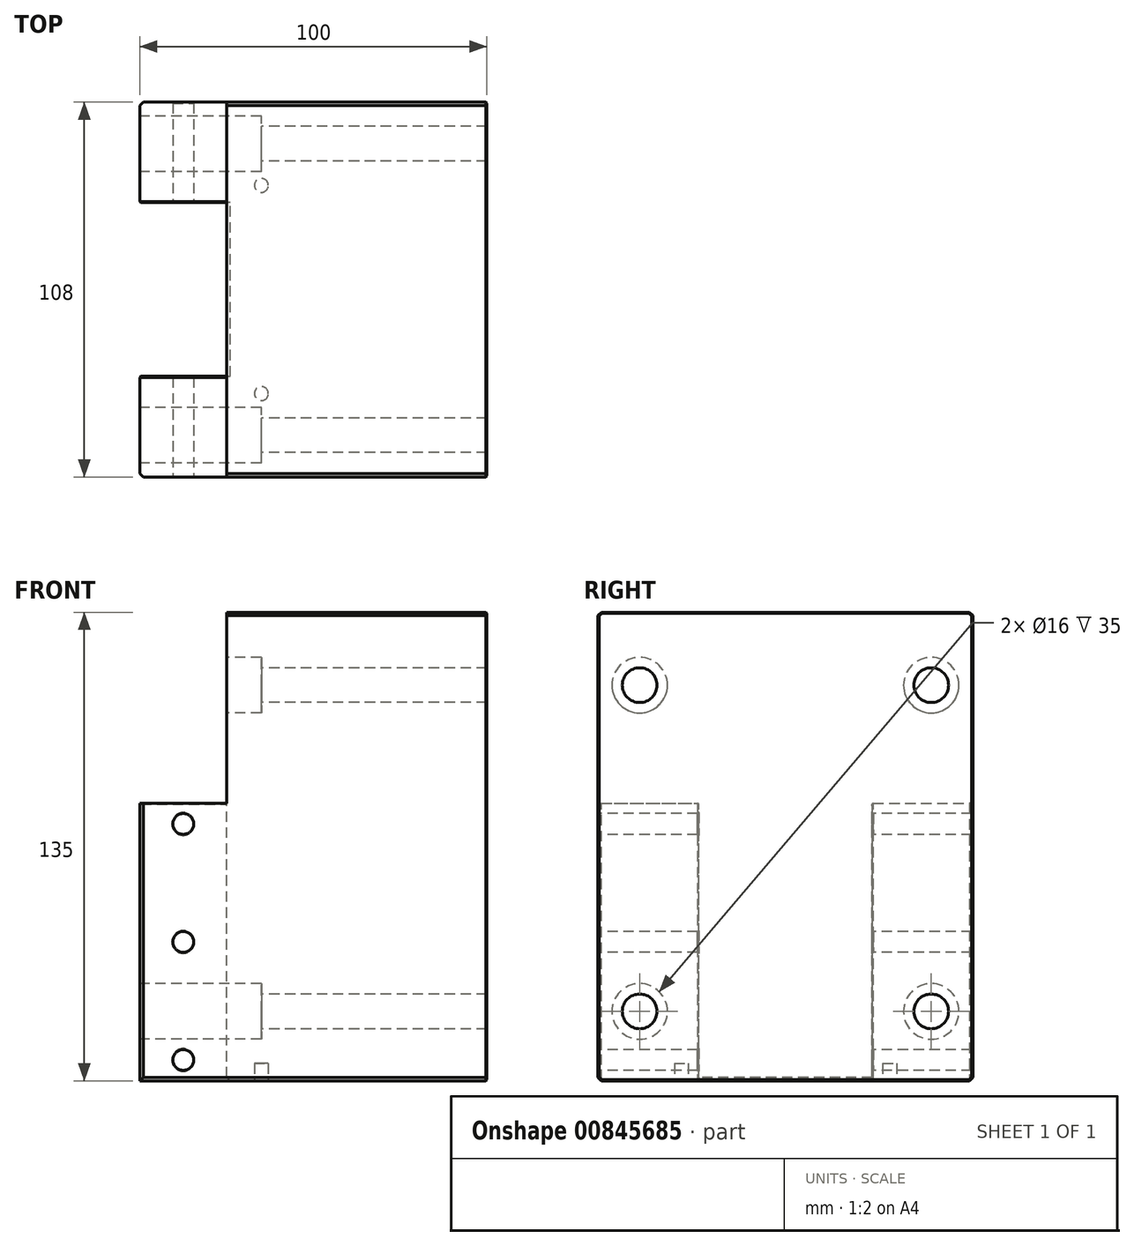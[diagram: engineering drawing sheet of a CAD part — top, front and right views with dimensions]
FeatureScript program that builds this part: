
annotation { "Feature Type Name" : "Feature", "Feature Type Description" : "" }
export const myFeature = defineFeature(function(context is Context, id is Id, definition is map)
    precondition{}
    {
        {
            var Q0;
            Q0=qCreatedBy(makeId("Front.planeOp"),FACE);
            var sketch = newSketch(context, id + "F0", { "sketchPlane" : qUnion([Q0])});
            skLineSegment(sketch, "E0.bottom", {"start": v(-100, -50) * mm, "end": v(-100, 58) * mm});
            skLineSegment(sketch, "E0.top", {"start": v(0, -50) * mm, "end": v(0, -21) * mm});
            skLineSegment(sketch, "E0.left", {"start": v(-100, -50) * mm, "end": v(0, -50) * mm});
            skLineSegment(sketch, "E0.right", {"start": v(-100, 58) * mm, "end": v(0, 58) * mm});
            skLineSegment(sketch, "E1", {"start": v(0, -21) * mm, "end": v(-25, -21) * mm});
            skLineSegment(sketch, "E2", {"start": v(-25, -21) * mm, "end": v(-25, 29) * mm});
            skLineSegment(sketch, "E3", {"start": v(-25, 29) * mm, "end": v(0, 29) * mm});
            skLineSegment(sketch, "E4.trimOffspring", {"start": v(0, 29) * mm, "end": v(0, 58) * mm});
            skLineSegment(sketch, "E5", {"start": v(0, -21) * mm, "end": v(0, 29) * mm, "construction": true});
            skSolve(sketch);
        }
        {
            var Q0;
            Q0 = qSketchRegion(id + "F0", true);
            extrude(context, id + "F1", {"entities" : qUnion([Q0]), "depth" : 135 * mm, "offsetDistance" : 25 * mm});
        }
        {
            var Q0;
            Q0=makeQuery(id+"F1.opExtrude","CAP_FACE",FACE,{"disambiguationData":[OSD([sQuery(id+"F0.wireOp",EDGE,"E0.bottom"),sQuery(id+"F0.wireOp",EDGE,"E0.top"),sQuery(id+"F0.wireOp",EDGE,"E0.left"),sQuery(id+"F0.wireOp",EDGE,"E0.right"),sQuery(id+"F0.wireOp",EDGE,"E1"),sQuery(id+"F0.wireOp",EDGE,"E2"),sQuery(id+"F0.wireOp",EDGE,"E3"),sQuery(id+"F0.wireOp",EDGE,"E4.trimOffspring")])],"isStart":true});
            var sketch = newSketch(context, id + "F2", { "sketchPlane" : qUnion([Q0])});
            skPoint(sketch, "E6.oppositeSnap0", {"position": v(25, 0) * mm});
            skLineSegment(sketch, "E6.bottom", {"start": v(0, -50) * mm, "end": v(0, 58) * mm});
            skLineSegment(sketch, "E6.top", {"start": v(25, -50) * mm, "end": v(25, 58) * mm});
            skLineSegment(sketch, "E6.left", {"start": v(25, -50) * mm, "end": v(0, -50) * mm});
            skLineSegment(sketch, "E6.right", {"start": v(25, 58) * mm, "end": v(0, 58) * mm});
            skSolve(sketch);
        }
        {
            var Q0;
            Q0 = qSketchRegion(id + "F2", true);
            extrude(context, id + "F3", {"entities" : qUnion([Q0]), "operationType" : NewBodyOperationType.REMOVE, "oppositeDirection" : true, "depth" : 55 * mm, "offsetDistance" : 25 * mm});
        }
        {
            var Q0;
            Q0=makeQuery(id+"F1.opExtrude","SWEPT_FACE",FACE,{"disambiguationData":[OSD([sQuery(id+"F0.wireOp",EDGE,"E0.top")])]});
            var sketch = newSketch(context, id + "F4", { "sketchPlane" : qUnion([Q0])});
            skCircle(sketch, "E7", {"center": v(-21, -38) * mm, "radius": 8 * mm});
            skCircle(sketch, "E8", {"center": v(-21, 46) * mm, "radius": 8 * mm});
            skCircle(sketch, "E9", {"center": v(-115, -38) * mm, "radius": 8 * mm});
            skCircle(sketch, "E10", {"center": v(-115, 46) * mm, "radius": 8 * mm});
            skLineSegment(sketch, "E11", {"start": v(-21, -38) * mm, "end": v(-115, -38) * mm, "construction": true});
            skLineSegment(sketch, "E12", {"start": v(-21, -38) * mm, "end": v(-21, 46) * mm, "construction": true});
            skLineSegment(sketch, "E13", {"start": v(-21, 46) * mm, "end": v(-115, 46) * mm, "construction": true});
            skLineSegment(sketch, "E14", {"start": v(-115, -38) * mm, "end": v(-115, 82.74) * mm, "construction": true});
            skSolve(sketch);
        }
        {
            var Q0;
            Q0 = qSketchRegion(id + "F4", true);
            extrude(context, id + "F5", {"entities" : qUnion([Q0]), "operationType" : NewBodyOperationType.REMOVE, "oppositeDirection" : true, "depth" : 35 * mm, "offsetDistance" : 25 * mm});
        }
        {
            var Q0;
            Q0=makeQuery(id+"F1.opExtrude","SWEPT_FACE",FACE,{"disambiguationData":[OSD([sQuery(id+"F0.wireOp",EDGE,"E0.left")])]});
            var sketch = newSketch(context, id + "F6", { "sketchPlane" : qUnion([Q0])});
            skPoint(sketch, "E15", {"position": v(-12.5, 61) * mm});
            skLineSegment(sketch, "E16", {"start": v(-12.5, 61) * mm, "end": v(-12.5, 68.08) * mm, "construction": true});
            skPoint(sketch, "E17", {"position": v(-12.5, 95) * mm});
            skPoint(sketch, "E18", {"position": v(-12.5, 129) * mm});
            skCircle(sketch, "E19", {"center": v(-12.5, 61) * mm, "radius": 3 * mm});
            skCircle(sketch, "E20", {"center": v(-12.5, 95) * mm, "radius": 3 * mm});
            skCircle(sketch, "E21", {"center": v(-12.5, 129) * mm, "radius": 3 * mm});
            skSolve(sketch);
        }
        {
            var Q0;
            Q0 = qSketchRegion(id + "F6", true);
            extrude(context, id + "F7", {"entities" : qUnion([Q0]), "operationType" : NewBodyOperationType.REMOVE, "endBound" : BoundingType.THROUGH_ALL, "oppositeDirection" : true, "depth" : 25 * mm, "offsetDistance" : 25 * mm});
        }
        {
            var Q0;
            Q0=makeQuery(id+"F1.opExtrude","CAP_FACE",FACE,{"disambiguationData":[OSD([sQuery(id+"F0.wireOp",EDGE,"E0.bottom"),sQuery(id+"F0.wireOp",EDGE,"E0.top"),sQuery(id+"F0.wireOp",EDGE,"E0.left"),sQuery(id+"F0.wireOp",EDGE,"E0.right"),sQuery(id+"F0.wireOp",EDGE,"E1"),sQuery(id+"F0.wireOp",EDGE,"E2"),sQuery(id+"F0.wireOp",EDGE,"E3"),sQuery(id+"F0.wireOp",EDGE,"E4.trimOffspring")])],"isStart":false});
            var sketch = newSketch(context, id + "F8", { "sketchPlane" : qUnion([Q0])});
            skLineSegment(sketch, "E22", {"start": v(-35, 34) * mm, "end": v(-35, -26) * mm, "construction": true});
            skPoint(sketch, "E23", {"position": v(-35, -26) * mm});
            skPoint(sketch, "E24", {"position": v(-35, 34) * mm});
            skCircle(sketch, "E25", {"center": v(-35, -26) * mm, "radius": 2 * mm});
            skCircle(sketch, "E26", {"center": v(-35, 34) * mm, "radius": 2 * mm});
            skSolve(sketch);
        }
        {
            var Q0;
            Q0 = qSketchRegion(id + "F8", true);
            extrude(context, id + "F9", {"entities" : qUnion([Q0]), "operationType" : NewBodyOperationType.REMOVE, "oppositeDirection" : true, "depth" : 5 * mm, "offsetDistance" : 25 * mm});
        }
        {
            var Q0;
            Q0=makeQuery(id+"F1.opExtrude","SWEPT_FACE",FACE,{"disambiguationData":[OSD([sQuery(id+"F0.wireOp",EDGE,"E4.trimOffspring")])]});
            var sketch = newSketch(context, id + "F10", { "sketchPlane" : qUnion([Q0])});
            skCircle(sketch, "E27", {"center": v(-115, 46) * mm, "radius": 5 * mm});
            skCircle(sketch, "E28", {"center": v(-21, 46) * mm, "radius": 5 * mm});
            skCircle(sketch, "E29", {"center": v(-21, -38) * mm, "radius": 5 * mm});
            skCircle(sketch, "E30", {"center": v(-115, -38) * mm, "radius": 5 * mm});
            skSolve(sketch);
        }
        {
            var Q0;
            Q0 = qSketchRegion(id + "F10", true);
            extrude(context, id + "F11", {"entities" : qUnion([Q0]), "operationType" : NewBodyOperationType.REMOVE, "endBound" : BoundingType.THROUGH_ALL, "oppositeDirection" : true, "depth" : 25 * mm, "offsetDistance" : 25 * mm});
        }
        {
            var Q0;
            Q0=makeQuery(id+"F1.opExtrude","CAP_EDGE",EDGE,{"disambiguationData":[OSD([sQuery(id+"F0.wireOp",EDGE,"E0.top")])],"isStart":true});
            var Q1;
            Q1=makeQuery(id+"F1.opExtrude","SWEPT_EDGE",EDGE,{"disambiguationData":[OSD([sQuery(id+"F0.wireOp",EDGE,"E0.top"),sQuery(id+"F0.wireOp",EDGE,"E0.left")])]});
            var Q2;
            {var subQ0=sQuery(id+"F2.wireOp",EDGE,"E6.bottom");Q2=makeQuery(id+"F3.boolean.opBoolean","COPY",EDGE,{"disambiguationData":[topologyDisambiguationEdgeConnected([makeQuery(id+"F1.opExtrude","SWEPT_FACE",FACE,{"disambiguationData":[OSD([sQuery(id+"F0.wireOp",EDGE,"E0.top")])]})])],"derivedFrom":makeQuery(id+"F3.opExtrude","CAP_EDGE",EDGE,{"disambiguationData":[OSD([subQ0])],"isStart":false})});}
            var Q3;
            Q3=makeQuery(id+"F3.boolean.opBoolean","COPY",EDGE,{"derivedFrom":makeQuery(id+"F3.opExtrude","SWEPT_EDGE",EDGE,{"disambiguationData":[OSD([sQuery(id+"F0.wireOp",EDGE,"E0.left"),sQuery(id+"F2.wireOp",EDGE,"E6.top"),sQuery(id+"F2.wireOp",EDGE,"E6.left")])]})});
            var Q4;
            Q4=makeQuery(id+"F3.boolean.opBoolean","MERGE",EDGE,{"derivedFrom":[makeQuery(id+"F1.opExtrude","CAP_EDGE",EDGE,{"disambiguationData":[OSD([sQuery(id+"F0.wireOp",EDGE,"E2")])],"isStart":false}),makeQuery(id+"F3.opExtrude","CAP_EDGE",EDGE,{"disambiguationData":[OSD([sQuery(id+"F2.wireOp",EDGE,"E6.top")])],"isStart":true})]});
            var Q5;
            Q5=makeQuery(id+"F3.boolean.opBoolean","COPY",EDGE,{"derivedFrom":makeQuery(id+"F3.opExtrude","SWEPT_EDGE",EDGE,{"disambiguationData":[OSD([sQuery(id+"F0.wireOp",EDGE,"E0.right"),sQuery(id+"F2.wireOp",EDGE,"E6.top"),sQuery(id+"F2.wireOp",EDGE,"E6.right")])]})});
            var Q6;
            Q6=makeQuery(id+"F3.boolean.opBoolean","COPY",EDGE,{"derivedFrom":makeQuery(id+"F3.opExtrude","CAP_EDGE",EDGE,{"disambiguationData":[OSD([sQuery(id+"F2.wireOp",EDGE,"E6.right")])],"isStart":false})});
            var Q7;
            {var subQ0=sQuery(id+"F2.wireOp",EDGE,"E6.bottom");Q7=makeQuery(id+"F3.boolean.opBoolean","COPY",EDGE,{"disambiguationData":[topologyDisambiguationEdgeConnected([makeQuery(id+"F1.opExtrude","SWEPT_FACE",FACE,{"disambiguationData":[OSD([sQuery(id+"F0.wireOp",EDGE,"E4.trimOffspring")])]})])],"derivedFrom":makeQuery(id+"F3.opExtrude","CAP_EDGE",EDGE,{"disambiguationData":[OSD([subQ0])],"isStart":false})});}
            var Q8;
            Q8=makeQuery(id+"F1.opExtrude","SWEPT_EDGE",EDGE,{"disambiguationData":[OSD([sQuery(id+"F0.wireOp",EDGE,"E0.right"),sQuery(id+"F0.wireOp",EDGE,"E4.trimOffspring")])]});
            var Q9;
            Q9=makeQuery(id+"F1.opExtrude","CAP_EDGE",EDGE,{"disambiguationData":[OSD([sQuery(id+"F0.wireOp",EDGE,"E4.trimOffspring")])],"isStart":true});
            var Q10;
            Q10=makeQuery(id+"F1.opExtrude","CAP_EDGE",EDGE,{"disambiguationData":[OSD([sQuery(id+"F0.wireOp",EDGE,"E0.right")])],"isStart":true});
            var Q11;
            Q11=makeQuery(id+"F1.opExtrude","CAP_EDGE",EDGE,{"disambiguationData":[OSD([sQuery(id+"F0.wireOp",EDGE,"E0.left")])],"isStart":true});
            var Q12;
            Q12=makeQuery(id+"F1.opExtrude","CAP_EDGE",EDGE,{"disambiguationData":[OSD([sQuery(id+"F0.wireOp",EDGE,"E0.right")])],"isStart":false});
            var Q13;
            Q13=makeQuery(id+"F1.opExtrude","CAP_EDGE",EDGE,{"disambiguationData":[OSD([sQuery(id+"F0.wireOp",EDGE,"E0.left")])],"isStart":false});
            var Q14;
            Q14=makeQuery(id+"F3.boolean.opBoolean","COPY",EDGE,{"derivedFrom":makeQuery(id+"F3.opExtrude","CAP_EDGE",EDGE,{"disambiguationData":[OSD([sQuery(id+"F2.wireOp",EDGE,"E6.left")])],"isStart":false})});
            chamfer(context, id + "F12", {"entities" : qUnion([Q0, Q1, Q2, Q3, Q4, Q5, Q6, Q7, Q8, Q9, Q10, Q11, Q12, Q13, Q14]), "width" : 1 * mm, "tangentPropagation" : true});
        }
        {
            var Q0;
            Q0=makeQuery(id+"F1.opExtrude","CAP_EDGE",EDGE,{"disambiguationData":[OSD([sQuery(id+"F0.wireOp",EDGE,"E1")])],"isStart":true});
            var Q1;
            Q1=makeQuery(id+"F12.opChamfer","BLEND_EDGE",EDGE,{"blendedFrom":[makeQuery(id+"F1.opExtrude","CAP_EDGE",EDGE,{"disambiguationData":[OSD([sQuery(id+"F0.wireOp",EDGE,"E0.top")])],"isStart":true}),makeQuery(id+"F1.opExtrude","SWEPT_FACE",FACE,{"disambiguationData":[OSD([sQuery(id+"F0.wireOp",EDGE,"E1")])]})],"blendedInto":[makeQuery(id+"F1.opExtrude","SWEPT_FACE",FACE,{"disambiguationData":[OSD([sQuery(id+"F0.wireOp",EDGE,"E1")])]})]});
            var Q2;
            Q2=makeQuery(id+"F1.opExtrude","SWEPT_EDGE",EDGE,{"disambiguationData":[OSD([sQuery(id+"F0.wireOp",EDGE,"E0.top"),sQuery(id+"F0.wireOp",EDGE,"E1")])]});
            var Q3;
            {var subQ0=sQuery(id+"F2.wireOp",EDGE,"E6.bottom");Q3=makeQuery(id+"F12.opChamfer","BLEND_EDGE",EDGE,{"blendedFrom":[makeQuery(id+"F3.boolean.opBoolean","COPY",EDGE,{"disambiguationData":[topologyDisambiguationEdgeConnected([makeQuery(id+"F1.opExtrude","SWEPT_FACE",FACE,{"disambiguationData":[OSD([sQuery(id+"F0.wireOp",EDGE,"E0.top")])]})])],"derivedFrom":makeQuery(id+"F3.opExtrude","CAP_EDGE",EDGE,{"disambiguationData":[OSD([subQ0])],"isStart":false})}),makeQuery(id+"F1.opExtrude","SWEPT_FACE",FACE,{"disambiguationData":[OSD([sQuery(id+"F0.wireOp",EDGE,"E1")])]})],"blendedInto":[makeQuery(id+"F1.opExtrude","SWEPT_FACE",FACE,{"disambiguationData":[OSD([sQuery(id+"F0.wireOp",EDGE,"E1")])]})]});}
            var Q4;
            Q4=makeQuery(id+"F3.boolean.opBoolean","INTERSECT",EDGE,{"derivedFrom":[makeQuery(id+"F1.opExtrude","SWEPT_FACE",FACE,{"disambiguationData":[OSD([sQuery(id+"F0.wireOp",EDGE,"E1")])]}),makeQuery(id+"F3.opExtrude","CAP_FACE",FACE,{"disambiguationData":[OSD([sQuery(id+"F2.wireOp",EDGE,"E6.bottom"),sQuery(id+"F2.wireOp",EDGE,"E6.top"),sQuery(id+"F2.wireOp",EDGE,"E6.left"),sQuery(id+"F2.wireOp",EDGE,"E6.right")])],"isStart":false})]});
            var Q5;
            Q5=makeQuery(id+"F3.boolean.opBoolean","INTERSECT",EDGE,{"derivedFrom":[makeQuery(id+"F1.opExtrude","SWEPT_FACE",FACE,{"disambiguationData":[OSD([sQuery(id+"F0.wireOp",EDGE,"E3")])]}),makeQuery(id+"F3.opExtrude","CAP_FACE",FACE,{"disambiguationData":[OSD([sQuery(id+"F2.wireOp",EDGE,"E6.bottom"),sQuery(id+"F2.wireOp",EDGE,"E6.top"),sQuery(id+"F2.wireOp",EDGE,"E6.left"),sQuery(id+"F2.wireOp",EDGE,"E6.right")])],"isStart":false})]});
            var Q6;
            {var subQ0=sQuery(id+"F2.wireOp",EDGE,"E6.bottom");Q6=makeQuery(id+"F12.opChamfer","BLEND_EDGE",EDGE,{"blendedFrom":[makeQuery(id+"F3.boolean.opBoolean","COPY",EDGE,{"disambiguationData":[topologyDisambiguationEdgeConnected([makeQuery(id+"F1.opExtrude","SWEPT_FACE",FACE,{"disambiguationData":[OSD([sQuery(id+"F0.wireOp",EDGE,"E4.trimOffspring")])]})])],"derivedFrom":makeQuery(id+"F3.opExtrude","CAP_EDGE",EDGE,{"disambiguationData":[OSD([subQ0])],"isStart":false})}),makeQuery(id+"F1.opExtrude","SWEPT_FACE",FACE,{"disambiguationData":[OSD([sQuery(id+"F0.wireOp",EDGE,"E3")])]})],"blendedInto":[makeQuery(id+"F1.opExtrude","SWEPT_FACE",FACE,{"disambiguationData":[OSD([sQuery(id+"F0.wireOp",EDGE,"E3")])]})]});}
            var Q7;
            Q7=makeQuery(id+"F1.opExtrude","SWEPT_EDGE",EDGE,{"disambiguationData":[OSD([sQuery(id+"F0.wireOp",EDGE,"E3"),sQuery(id+"F0.wireOp",EDGE,"E4.trimOffspring")])]});
            var Q8;
            Q8=makeQuery(id+"F12.opChamfer","BLEND_EDGE",EDGE,{"blendedFrom":[makeQuery(id+"F1.opExtrude","CAP_EDGE",EDGE,{"disambiguationData":[OSD([sQuery(id+"F0.wireOp",EDGE,"E4.trimOffspring")])],"isStart":true}),makeQuery(id+"F1.opExtrude","SWEPT_FACE",FACE,{"disambiguationData":[OSD([sQuery(id+"F0.wireOp",EDGE,"E3")])]})],"blendedInto":[makeQuery(id+"F1.opExtrude","SWEPT_FACE",FACE,{"disambiguationData":[OSD([sQuery(id+"F0.wireOp",EDGE,"E3")])]})]});
            var Q9;
            Q9=makeQuery(id+"F1.opExtrude","CAP_EDGE",EDGE,{"disambiguationData":[OSD([sQuery(id+"F0.wireOp",EDGE,"E3")])],"isStart":true});
            var Q10;
            Q10=makeQuery(id+"F5.boolean.opBoolean","COPY",EDGE,{"derivedFrom":makeQuery(id+"F5.opExtrude","CAP_EDGE",EDGE,{"disambiguationData":[OSD([sQuery(id+"F4.wireOp",EDGE,"E8")])],"isStart":true})});
            var Q11;
            Q11=makeQuery(id+"F5.boolean.opBoolean","COPY",EDGE,{"derivedFrom":makeQuery(id+"F5.opExtrude","CAP_EDGE",EDGE,{"disambiguationData":[OSD([sQuery(id+"F4.wireOp",EDGE,"E7")])],"isStart":true})});
            var Q12;
            Q12=makeQuery(id+"F5.boolean.opBoolean","INTERSECT",EDGE,{"derivedFrom":[makeQuery(id+"F3.boolean.opBoolean","MERGE",FACE,{"derivedFrom":[makeQuery(id+"F1.opExtrude","SWEPT_FACE",FACE,{"disambiguationData":[OSD([sQuery(id+"F0.wireOp",EDGE,"E2")])]}),makeQuery(id+"F3.opExtrude","SWEPT_FACE",FACE,{"disambiguationData":[OSD([sQuery(id+"F2.wireOp",EDGE,"E6.top")])]})]}),makeQuery(id+"F5.opExtrude","SWEPT_FACE",FACE,{"disambiguationData":[OSD([sQuery(id+"F4.wireOp",EDGE,"E9")])]})]});
            var Q13;
            Q13=makeQuery(id+"F5.boolean.opBoolean","INTERSECT",EDGE,{"derivedFrom":[makeQuery(id+"F3.boolean.opBoolean","MERGE",FACE,{"derivedFrom":[makeQuery(id+"F1.opExtrude","SWEPT_FACE",FACE,{"disambiguationData":[OSD([sQuery(id+"F0.wireOp",EDGE,"E2")])]}),makeQuery(id+"F3.opExtrude","SWEPT_FACE",FACE,{"disambiguationData":[OSD([sQuery(id+"F2.wireOp",EDGE,"E6.top")])]})]}),makeQuery(id+"F5.opExtrude","SWEPT_FACE",FACE,{"disambiguationData":[OSD([sQuery(id+"F4.wireOp",EDGE,"E10")])]})]});
            var Q14;
            Q14=makeQuery(id+"F7.boolean.opBoolean","INTERSECT",EDGE,{"derivedFrom":[makeQuery(id+"F1.opExtrude","SWEPT_FACE",FACE,{"disambiguationData":[OSD([sQuery(id+"F0.wireOp",EDGE,"E3")])]}),makeQuery(id+"F7.opExtrude","SWEPT_FACE",FACE,{"disambiguationData":[OSD([sQuery(id+"F6.wireOp",EDGE,"E21")])]})]});
            var Q15;
            Q15=makeQuery(id+"F7.boolean.opBoolean","INTERSECT",EDGE,{"derivedFrom":[makeQuery(id+"F1.opExtrude","SWEPT_FACE",FACE,{"disambiguationData":[OSD([sQuery(id+"F0.wireOp",EDGE,"E3")])]}),makeQuery(id+"F7.opExtrude","SWEPT_FACE",FACE,{"disambiguationData":[OSD([sQuery(id+"F6.wireOp",EDGE,"E20")])]})]});
            var Q16;
            Q16=makeQuery(id+"F7.boolean.opBoolean","INTERSECT",EDGE,{"derivedFrom":[makeQuery(id+"F1.opExtrude","SWEPT_FACE",FACE,{"disambiguationData":[OSD([sQuery(id+"F0.wireOp",EDGE,"E3")])]}),makeQuery(id+"F7.opExtrude","SWEPT_FACE",FACE,{"disambiguationData":[OSD([sQuery(id+"F6.wireOp",EDGE,"E19")])]})]});
            var Q17;
            Q17=makeQuery(id+"F7.boolean.opBoolean","INTERSECT",EDGE,{"derivedFrom":[makeQuery(id+"F1.opExtrude","SWEPT_FACE",FACE,{"disambiguationData":[OSD([sQuery(id+"F0.wireOp",EDGE,"E1")])]}),makeQuery(id+"F7.opExtrude","SWEPT_FACE",FACE,{"disambiguationData":[OSD([sQuery(id+"F6.wireOp",EDGE,"E19")])]})]});
            var Q18;
            Q18=makeQuery(id+"F7.boolean.opBoolean","INTERSECT",EDGE,{"derivedFrom":[makeQuery(id+"F1.opExtrude","SWEPT_FACE",FACE,{"disambiguationData":[OSD([sQuery(id+"F0.wireOp",EDGE,"E1")])]}),makeQuery(id+"F7.opExtrude","SWEPT_FACE",FACE,{"disambiguationData":[OSD([sQuery(id+"F6.wireOp",EDGE,"E20")])]})]});
            var Q19;
            Q19=makeQuery(id+"F7.boolean.opBoolean","INTERSECT",EDGE,{"derivedFrom":[makeQuery(id+"F1.opExtrude","SWEPT_FACE",FACE,{"disambiguationData":[OSD([sQuery(id+"F0.wireOp",EDGE,"E1")])]}),makeQuery(id+"F7.opExtrude","SWEPT_FACE",FACE,{"disambiguationData":[OSD([sQuery(id+"F6.wireOp",EDGE,"E21")])]})]});
            var Q20;
            Q20=makeQuery(id+"F7.boolean.opBoolean","INTERSECT",EDGE,{"derivedFrom":[makeQuery(id+"F1.opExtrude","SWEPT_FACE",FACE,{"disambiguationData":[OSD([sQuery(id+"F0.wireOp",EDGE,"E0.right")])]}),makeQuery(id+"F7.opExtrude","SWEPT_FACE",FACE,{"disambiguationData":[OSD([sQuery(id+"F6.wireOp",EDGE,"E20")])]})]});
            var Q21;
            Q21=makeQuery(id+"F7.boolean.opBoolean","INTERSECT",EDGE,{"derivedFrom":[makeQuery(id+"F1.opExtrude","SWEPT_FACE",FACE,{"disambiguationData":[OSD([sQuery(id+"F0.wireOp",EDGE,"E0.right")])]}),makeQuery(id+"F7.opExtrude","SWEPT_FACE",FACE,{"disambiguationData":[OSD([sQuery(id+"F6.wireOp",EDGE,"E19")])]})]});
            var Q22;
            Q22=makeQuery(id+"F7.boolean.opBoolean","INTERSECT",EDGE,{"derivedFrom":[makeQuery(id+"F1.opExtrude","SWEPT_FACE",FACE,{"disambiguationData":[OSD([sQuery(id+"F0.wireOp",EDGE,"E0.right")])]}),makeQuery(id+"F7.opExtrude","SWEPT_FACE",FACE,{"disambiguationData":[OSD([sQuery(id+"F6.wireOp",EDGE,"E21")])]})]});
            var Q23;
            Q23=makeQuery(id+"F1.opExtrude","SWEPT_EDGE",EDGE,{"disambiguationData":[OSD([sQuery(id+"F0.wireOp",EDGE,"E0.bottom"),sQuery(id+"F0.wireOp",EDGE,"E0.right")])]});
            var Q24;
            Q24=makeQuery(id+"F7.boolean.opBoolean","COPY",EDGE,{"derivedFrom":makeQuery(id+"F7.opExtrude","CAP_EDGE",EDGE,{"disambiguationData":[OSD([sQuery(id+"F6.wireOp",EDGE,"E21")])],"isStart":true})});
            var Q25;
            Q25=makeQuery(id+"F7.boolean.opBoolean","COPY",EDGE,{"derivedFrom":makeQuery(id+"F7.opExtrude","CAP_EDGE",EDGE,{"disambiguationData":[OSD([sQuery(id+"F6.wireOp",EDGE,"E20")])],"isStart":true})});
            var Q26;
            Q26=makeQuery(id+"F7.boolean.opBoolean","COPY",EDGE,{"derivedFrom":makeQuery(id+"F7.opExtrude","CAP_EDGE",EDGE,{"disambiguationData":[OSD([sQuery(id+"F6.wireOp",EDGE,"E19")])],"isStart":true})});
            var Q27;
            Q27=makeQuery(id+"F1.opExtrude","SWEPT_EDGE",EDGE,{"disambiguationData":[OSD([sQuery(id+"F0.wireOp",EDGE,"E0.bottom"),sQuery(id+"F0.wireOp",EDGE,"E0.left")])]});
            var Q28;
            Q28=makeQuery(id+"F1.opExtrude","CAP_EDGE",EDGE,{"disambiguationData":[OSD([sQuery(id+"F0.wireOp",EDGE,"E0.bottom")])],"isStart":true});
            var Q29;
            Q29=makeQuery(id+"F12.opChamfer","BLEND_EDGE",EDGE,{"blendedFrom":[makeQuery(id+"F1.opExtrude","CAP_EDGE",EDGE,{"disambiguationData":[OSD([sQuery(id+"F0.wireOp",EDGE,"E0.left")])],"isStart":true}),makeQuery(id+"F1.opExtrude","SWEPT_FACE",FACE,{"disambiguationData":[OSD([sQuery(id+"F0.wireOp",EDGE,"E0.bottom")])]})],"blendedInto":[makeQuery(id+"F1.opExtrude","SWEPT_FACE",FACE,{"disambiguationData":[OSD([sQuery(id+"F0.wireOp",EDGE,"E0.bottom")])]})]});
            var Q30;
            Q30=makeQuery(id+"F12.opChamfer","BLEND_EDGE",EDGE,{"blendedFrom":[makeQuery(id+"F1.opExtrude","CAP_EDGE",EDGE,{"disambiguationData":[OSD([sQuery(id+"F0.wireOp",EDGE,"E0.left")])],"isStart":false}),makeQuery(id+"F1.opExtrude","SWEPT_FACE",FACE,{"disambiguationData":[OSD([sQuery(id+"F0.wireOp",EDGE,"E0.bottom")])]})],"blendedInto":[makeQuery(id+"F1.opExtrude","SWEPT_FACE",FACE,{"disambiguationData":[OSD([sQuery(id+"F0.wireOp",EDGE,"E0.bottom")])]})]});
            var Q31;
            Q31=makeQuery(id+"F1.opExtrude","CAP_EDGE",EDGE,{"disambiguationData":[OSD([sQuery(id+"F0.wireOp",EDGE,"E0.bottom")])],"isStart":false});
            var Q32;
            Q32=makeQuery(id+"F12.opChamfer","BLEND_EDGE",EDGE,{"blendedFrom":[makeQuery(id+"F1.opExtrude","CAP_EDGE",EDGE,{"disambiguationData":[OSD([sQuery(id+"F0.wireOp",EDGE,"E0.right")])],"isStart":false}),makeQuery(id+"F1.opExtrude","SWEPT_FACE",FACE,{"disambiguationData":[OSD([sQuery(id+"F0.wireOp",EDGE,"E0.bottom")])]})],"blendedInto":[makeQuery(id+"F1.opExtrude","SWEPT_FACE",FACE,{"disambiguationData":[OSD([sQuery(id+"F0.wireOp",EDGE,"E0.bottom")])]})]});
            var Q33;
            Q33=makeQuery(id+"F12.opChamfer","BLEND_EDGE",EDGE,{"blendedFrom":[makeQuery(id+"F1.opExtrude","CAP_EDGE",EDGE,{"disambiguationData":[OSD([sQuery(id+"F0.wireOp",EDGE,"E0.right")])],"isStart":true}),makeQuery(id+"F1.opExtrude","SWEPT_FACE",FACE,{"disambiguationData":[OSD([sQuery(id+"F0.wireOp",EDGE,"E0.bottom")])]})],"blendedInto":[makeQuery(id+"F1.opExtrude","SWEPT_FACE",FACE,{"disambiguationData":[OSD([sQuery(id+"F0.wireOp",EDGE,"E0.bottom")])]})]});
            var Q34;
            Q34=makeQuery(id+"F1.opExtrude","CAP_EDGE",EDGE,{"disambiguationData":[OSD([sQuery(id+"F0.wireOp",EDGE,"E2")])],"isStart":true});
            chamfer(context, id + "F13", {"entities" : qUnion([Q0, Q1, Q2, Q3, Q4, Q5, Q6, Q7, Q8, Q9, Q10, Q11, Q12, Q13, Q14, Q15, Q16, Q17, Q18, Q19, Q20, Q21, Q22, Q23, Q24, Q25, Q26, Q27, Q28, Q29, Q30, Q31, Q32, Q33, Q34]), "width" : 0.3 * mm, "tangentPropagation" : true});
        }
        {
            var Q0;
            Q0=makeQuery(id+"F1.opExtrude","SWEPT_BODY",BODY,{"disambiguationData":[OSD([sQuery(id+"F0.wireOp",EDGE,"E0.bottom"),sQuery(id+"F0.wireOp",EDGE,"E0.top"),sQuery(id+"F0.wireOp",EDGE,"E0.left"),sQuery(id+"F0.wireOp",EDGE,"E0.right"),sQuery(id+"F0.wireOp",EDGE,"E1"),sQuery(id+"F0.wireOp",EDGE,"E2"),sQuery(id+"F0.wireOp",EDGE,"E3"),sQuery(id+"F0.wireOp",EDGE,"E4.trimOffspring")])]});
            var Q1;
            {var subQ0=sQuery(id+"F0.wireOp",EDGE,"E4.trimOffspring");Q1=makeQuery(id+"F12.opChamfer","BLEND_EDGE",EDGE,{"blendedFrom":[makeQuery(id+"F1.opExtrude","SWEPT_EDGE",EDGE,{"disambiguationData":[OSD([sQuery(id+"F0.wireOp",EDGE,"E0.right"),subQ0])]}),makeQuery(id+"F1.opExtrude","SWEPT_FACE",FACE,{"disambiguationData":[OSD([subQ0])]})],"blendedInto":[makeQuery(id+"F1.opExtrude","SWEPT_FACE",FACE,{"disambiguationData":[OSD([subQ0])]})]});}
            transform(context, id + "F14", {"entities" : qUnion([Q0]), "transformType" : TransformType.ROTATION, "transformAxis" : qUnion([Q1]), "angle" : 180 * degree, "makeCopy" : false});
        }
        {
            var Q0;
            Q0=makeQuery(id+"F1.opExtrude","SWEPT_FACE",FACE,{"disambiguationData":[OSD([sQuery(id+"F0.wireOp",EDGE,"E0.bottom")])]});
            var sketch = newSketch(context, id + "F15", { "sketchPlane" : qUnion([Q0])});
            skLineSegment(sketch, "E31", {"start": v(-134.29, 56.71) * mm, "end": v(-0.71, 163.29) * mm, "construction": true});
            skLineSegment(sketch, "E32", {"start": v(-67.5, 110) * mm, "end": v(7.88, 10.49) * mm, "construction": true});
            skSolve(sketch);
        }
        {
            var Q0;
            Q0=makeQuery(id+"F1.opExtrude","SWEPT_BODY",BODY,{"disambiguationData":[OSD([sQuery(id+"F0.wireOp",EDGE,"E0.bottom"),sQuery(id+"F0.wireOp",EDGE,"E0.top"),sQuery(id+"F0.wireOp",EDGE,"E0.left"),sQuery(id+"F0.wireOp",EDGE,"E0.right"),sQuery(id+"F0.wireOp",EDGE,"E1"),sQuery(id+"F0.wireOp",EDGE,"E2"),sQuery(id+"F0.wireOp",EDGE,"E3"),sQuery(id+"F0.wireOp",EDGE,"E4.trimOffspring")])]});
            var Q1;
            Q1=sQuery(id+"F15.wireOp",EDGE,"E32");
            transform(context, id + "F16", {"entities" : qUnion([Q0]), "transformType" : TransformType.TRANSLATION_ENTITY, "oppositeDirectionEntity" : false, "transformLine" : qUnion([Q1]), "makeCopy" : false});
        }
        {
            var Q0;
            Q0=qCreatedBy(makeId("Front.planeOp"),FACE);
            var sketch = newSketch(context, id + "F17", { "sketchPlane" : qUnion([Q0])});
            skLineSegment(sketch, "E33", {"start": v(0, 0) * mm, "end": v(130.24, 0) * mm, "construction": true});
            skSolve(sketch);
        }
        {
            var Q0;
            Q0=makeQuery(id+"F1.opExtrude","SWEPT_BODY",BODY,{"disambiguationData":[OSD([sQuery(id+"F0.wireOp",EDGE,"E0.bottom"),sQuery(id+"F0.wireOp",EDGE,"E0.top"),sQuery(id+"F0.wireOp",EDGE,"E0.left"),sQuery(id+"F0.wireOp",EDGE,"E0.right"),sQuery(id+"F0.wireOp",EDGE,"E1"),sQuery(id+"F0.wireOp",EDGE,"E2"),sQuery(id+"F0.wireOp",EDGE,"E3"),sQuery(id+"F0.wireOp",EDGE,"E4.trimOffspring")])]});
            var Q1;
            Q1=sQuery(id+"F17.wireOp",EDGE,"E33");
            transform(context, id + "F18", {"entities" : qUnion([Q0]), "transformType" : TransformType.ROTATION, "transformAxis" : qUnion([Q1]), "angle" : 90 * degree, "makeCopy" : false});
        }
        {
            var Q0;
            Q0=makeQuery(id+"F1.opExtrude","SWEPT_FACE",FACE,{"disambiguationData":[OSD([sQuery(id+"F0.wireOp",EDGE,"E0.bottom")])]});
            var sketch = newSketch(context, id + "F19", { "sketchPlane" : qUnion([Q0])});
            skLineSegment(sketch, "E34", {"start": v(-10.49, -59.32) * mm, "end": v(-10.49, 75.08) * mm, "construction": true});
            skPoint(sketch, "E35", {"position": v(0, 0) * mm});
            skLineSegment(sketch, "E36", {"start": v(-10.49, 7.88) * mm, "end": v(0, 0) * mm, "construction": true});
            skSolve(sketch);
        }
        {
            var Q0;
            Q0=makeQuery(id+"F1.opExtrude","SWEPT_BODY",BODY,{"disambiguationData":[OSD([sQuery(id+"F0.wireOp",EDGE,"E0.bottom"),sQuery(id+"F0.wireOp",EDGE,"E0.top"),sQuery(id+"F0.wireOp",EDGE,"E0.left"),sQuery(id+"F0.wireOp",EDGE,"E0.right"),sQuery(id+"F0.wireOp",EDGE,"E1"),sQuery(id+"F0.wireOp",EDGE,"E2"),sQuery(id+"F0.wireOp",EDGE,"E3"),sQuery(id+"F0.wireOp",EDGE,"E4.trimOffspring")])]});
            var Q1;
            Q1=sQuery(id+"F19.wireOp",EDGE,"E36");
            transform(context, id + "F20", {"entities" : qUnion([Q0]), "transformType" : TransformType.TRANSLATION_ENTITY, "oppositeDirectionEntity" : false, "transformLine" : qUnion([Q1]), "makeCopy" : false});
        }
    });
